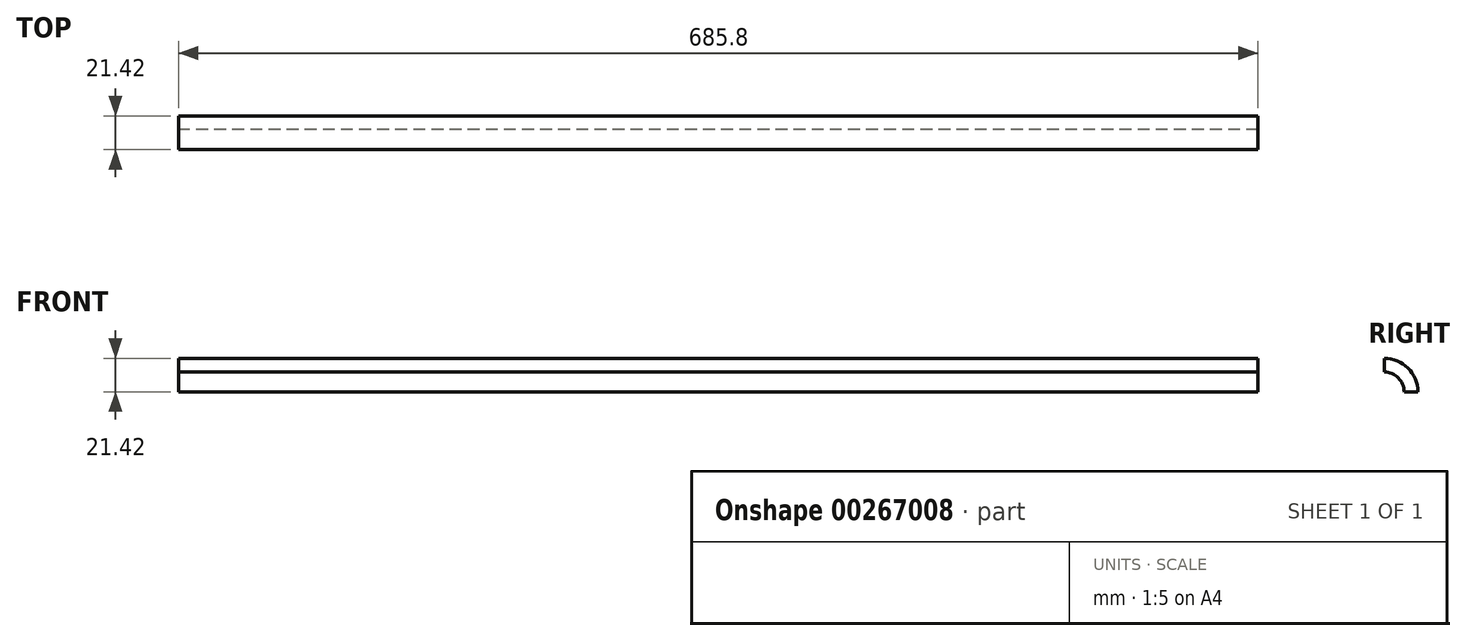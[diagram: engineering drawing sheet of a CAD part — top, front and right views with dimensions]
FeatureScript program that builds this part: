
annotation { "Feature Type Name" : "Feature", "Feature Type Description" : "" }
export const myFeature = defineFeature(function(context is Context, id is Id, definition is map)
    precondition{}
    {
        {
            var Q0;
            Q0=qCreatedBy(makeId("Right.planeOp"),FACE);
            var sketch = newSketch(context, id + "F0", { "sketchPlane" : qUnion([Q0])});
            skArc(sketch, "E0", {"start": v(12.7, 0) * mm, "mid": v(8.98, 8.98) * mm, "end": v(0, 12.7) * mm});
            skArc(sketch, "E1", {"start": v(21.42, 0) * mm, "mid": v(15.15, 15.15) * mm, "end": v(0, 21.42) * mm});
            skLineSegment(sketch, "E2", {"start": v(0, 21.42) * mm, "end": v(0, 12.7) * mm});
            skLineSegment(sketch, "E3", {"start": v(12.7, 0) * mm, "end": v(21.42, 0) * mm});
            skSolve(sketch);
        }
        {
            var Q0;
            Q0 = qSketchRegion(id + "F0", true);
            extrude(context, id + "F1", {"entities" : qUnion([Q0]), "depth" : 685.8 * mm});
        }
    });
